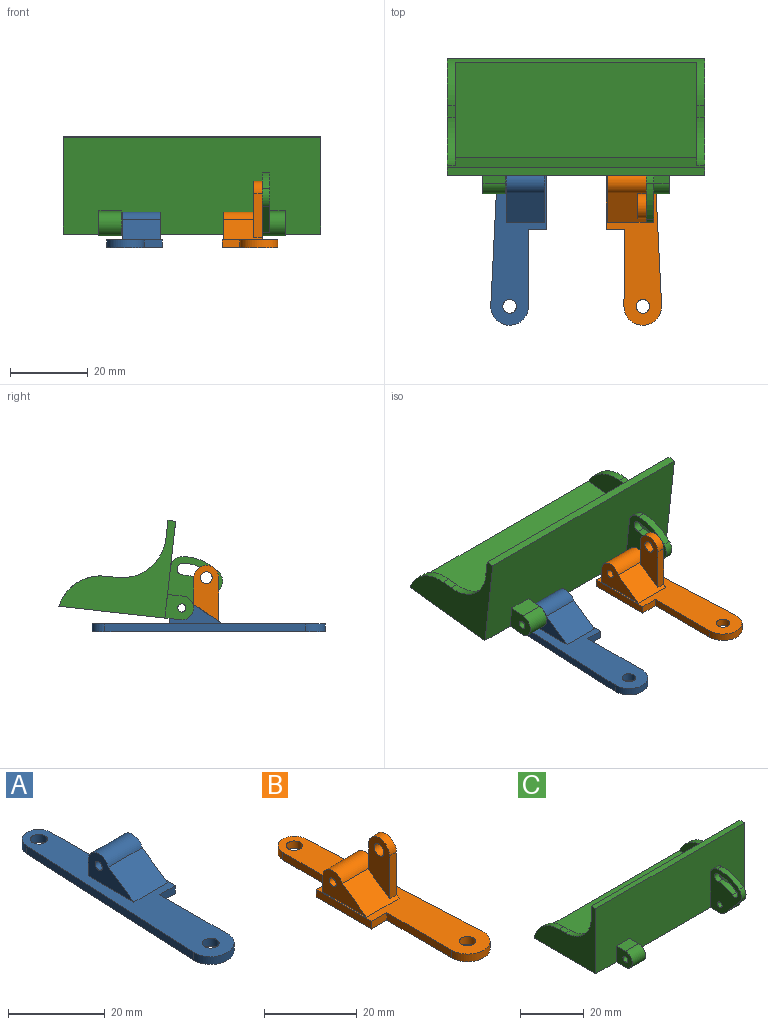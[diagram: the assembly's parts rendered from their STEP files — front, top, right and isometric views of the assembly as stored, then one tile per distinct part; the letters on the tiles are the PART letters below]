
ASSEMBLY  parts=3 mates=3
PART A: 18 faces, bbox 14.3x59.9x9.1 mm
  f0: plane 16.87x2mm, normal (1,0,0), area 33.7mm2, adj f1,f8,f10,f11
  f1: plane 4.68x2mm, normal (0,1,0), area 9.4mm2, adj f0,f2,f10,f11
  f2: plane 14.87x2mm, normal (1,0,0), area 29.7mm2, adj f1,f3,f10,f11
  f3: cylinder r=3.51mm len=7.01mm, axis (0,0,-1), area 21.7mm2, adj f2,f4,f10,f11
  f4: plane 51.47x2.53mm, normal (-1,0.05,0), area 103.1mm2, adj f3,f5,f10,f11
  f5: cylinder r=4.83mm len=9.67mm, axis (0,0,-1), area 30.9mm2, adj f4,f6,f10,f11
  f6: plane 19.79x2mm, normal (1,0,0), area 39.6mm2, adj f5,f8,f10,f11
  f7: cylinder r=1.75mm len=3.5mm, axis (0,0,-1), area 22mm2, adj f10,f11
  f8: plane 4.64x2mm, normal (0,-1,0), area 9.3mm2, adj f0,f6,f10,f11
  f9: cylinder r=1.75mm len=3.5mm, axis (0,0,-1), area 22mm2, adj f10,f11
  f10: plane 59.88x14.26mm, normal (0,0,1), area 413.1mm2, adj f0,f1,f2,f3,f4,f5,f6,f7
  f11: plane 59.88x14.26mm, normal (0,0,-1), area 545.5mm2, adj f0,f1,f2,f3,f4,f5,f6,f7
  f12: plane 9.9x4.05mm, normal (0,1,0), area 40.1mm2, adj f10,f14,f15,f16
  f13: cylinder r=1.05mm len=9.9mm, axis (1,0,0), area 65.3mm2, adj f15,f16
  f14: cylinder r=3.05mm len=9.9mm, axis (1,0,0), area 83.8mm2, adj f12,f15,f16,f17
  f15: plane 13.37x7.1mm, normal (-1,0,0), area 54.1mm2, adj f10,f12,f13,f14,f17
  f16: plane 13.37x7.1mm, normal (1,0,0), area 54.1mm2, adj f10,f12,f13,f14,f17
  f17: plane 9.9x7.47mm, normal (0,-0.57,0.82), area 89.8mm2, adj f10,f14,f15,f16
PART B: 23 faces, bbox 14.3x59.9x17 mm
  f0: plane 9.9x7.47mm, normal (0,-0.57,0.82), area 73.5mm2, adj f1,f15,f16,f17,f18,f19,f20
  f1: plane 59.88x14.26mm, normal (0,0,1), area 413.1mm2, adj f0,f2,f3,f4,f5,f6,f7,f8
  f2: plane 4.68x2mm, normal (0,1,0), area 9.4mm2, adj f1,f3,f10,f12
  f3: plane 16.87x2mm, normal (-1,0,0), area 33.7mm2, adj f1,f2,f4,f12
  f4: plane 4.64x2mm, normal (0,-1,0), area 9.3mm2, adj f1,f3,f5,f12
  f5: plane 19.79x2mm, normal (-1,0,0), area 39.6mm2, adj f1,f4,f6,f12
  f6: cylinder r=4.83mm len=9.67mm, axis (0,0,-1), area 30.9mm2, adj f1,f5,f7,f12
  f7: plane 51.47x2.53mm, normal (1,0.05,0), area 103.1mm2, adj f1,f6,f8,f12
  f8: cylinder r=3.51mm len=7.01mm, axis (0,0,-1), area 21.7mm2, adj f1,f7,f10,f12
  f9: cylinder r=1.75mm len=3.5mm, axis (0,0,-1), area 22mm2, adj f1,f12
  f10: plane 14.88x2mm, normal (-1,0,0), area 29.8mm2, adj f1,f2,f8,f12
  f11: cylinder r=1.75mm len=3.5mm, axis (0,0,-1), area 22mm2, adj f1,f12
  f12: plane 59.88x14.26mm, normal (0,0,-1), area 545.5mm2, adj f2,f3,f4,f5,f6,f7,f8,f9
  f13: plane 9.9x4.05mm, normal (0,1,0), area 40.1mm2, adj f1,f15,f16,f17
  f14: cylinder r=1.05mm len=9.9mm, axis (-1,0,0), area 65.3mm2, adj f16,f17
  f15: cylinder r=3.05mm len=9.9mm, axis (-1,0,0), area 83.8mm2, adj f0,f13,f16,f17
  f16: plane 15.02x13.37mm, normal (1,0,0), area 121mm2, adj f0,f1,f13,f14,f15,f18,f19,f21
  f17: plane 13.37x7.1mm, normal (-1,0,0), area 54.1mm2, adj f0,f1,f13,f14,f15
  f18: plane 6.85x2.1mm, normal (0,1,0), area 14.4mm2, adj f0,f16,f20,f21
  f19: plane 11.25x2.1mm, normal (0,-1,0), area 23.6mm2, adj f0,f16,f20,f21
  f20: plane 14.45x6.4mm, normal (-1,0,0), area 66.9mm2, adj f0,f18,f19,f21,f22
  f21: cylinder r=3.2mm len=6.4mm, axis (1,0,0), area 21.1mm2, adj f16,f18,f19,f20
  f22: cylinder r=1.5mm len=3mm, axis (1,0,0), area 19.8mm2, adj f16,f20
PART C: 33 faces, bbox 66x41.1x25 mm
  f0: plane 66x25mm, normal (0,-1,0), area 1564.2mm2, adj f1,f3,f4,f5,f7,f14,f15,f16
  f1: plane 4.05x3.9mm, normal (0,0,1), area 15.8mm2, adj f0,f12,f14,f32
  f2: plane 62x24.78mm, normal (0,0,1), area 1536.3mm2, adj f6,f8,f10,f22
  f3: plane 27.4x25mm, normal (-1,0,0), area 281mm2, adj f0,f5,f6,f7,f9,f22,f23
  f4: plane 27.4x25mm, normal (1,0,0), area 281mm2, adj f0,f5,f6,f7,f11,f21,f22
  f5: plane 66x31.45mm, normal (0,0,-1), area 1856.2mm2, adj f0,f3,f4,f12,f14,f15,f17,f19
  f6: plane 66x23mm, normal (0,1,0), area 1444.6mm2, adj f2,f3,f4,f7,f8,f10,f21,f23
  f7: plane 66x2mm, normal (0,0,1), area 132mm2, adj f0,f3,f4,f6
  f8: plane 24.78x18.35mm, normal (1,0,0), area 180.8mm2, adj f2,f6,f9,f22,f23
  f9: plane 2.95x2mm, normal (0,0,1), area 5.9mm2, adj f3,f8,f22,f23
  f10: plane 24.78x18.35mm, normal (-1,0,0), area 180.8mm2, adj f2,f6,f11,f21,f22
  f11: plane 2.95x2mm, normal (0,0,1), area 5.9mm2, adj f4,f10,f21,f22
  f12: cylinder r=3.05mm len=6.1mm, axis (-1,0,0), area 42.6mm2, adj f1,f5,f14,f15,f27,f32
  f13: cylinder r=1.05mm len=5.9mm, axis (-1,0,0), area 38.9mm2, adj f14,f15
  f14: plane 7.1x6.1mm, normal (1,0,0), area 35.9mm2, adj f0,f1,f5,f12,f13
  f15: plane 16.25x13.69mm, normal (-1,0,0), area 133.8mm2, adj f0,f5,f12,f13,f24,f25,f26,f27
  f16: plane 5.9x4.05mm, normal (0,0,1), area 23.9mm2, adj f0,f17,f19,f20
  f17: cylinder r=3.05mm len=6.1mm, axis (1,0,0), area 56.5mm2, adj f5,f16,f19,f20
  f18: cylinder r=1.05mm len=5.9mm, axis (1,0,0), area 38.9mm2, adj f19,f20
  f19: plane 7.1x6.1mm, normal (-1,0,0), area 35.9mm2, adj f0,f5,f16,f17,f18
  f20: plane 7.1x6.1mm, normal (1,0,0), area 35.9mm2, adj f0,f5,f16,f17,f18
  f21: cylinder r=11.35mm len=11.35mm, axis (-1,0,0), area 35.6mm2, adj f4,f6,f10,f11
  f22: cylinder r=11.35mm len=66mm, axis (-1,0,0), area 191.9mm2, adj f2,f3,f4,f5,f8,f9,f10,f11
  f23: cylinder r=11.35mm len=11.35mm, axis (1,0,0), area 35.6mm2, adj f3,f6,f8,f9
  f24: cylinder r=11.5mm len=8.39mm, axis (-1,0,0), area 18.1mm2, adj f15,f25,f31,f32
  f25: cylinder r=1.5mm len=2.65mm, axis (-1,0,0), area 9.4mm2, adj f15,f24,f26,f32
  f26: cylinder r=8.5mm len=6.2mm, axis (-1,0,0), area 13.4mm2, adj f15,f25,f31,f32
  f27: plane 7.55x6.56mm, normal (0,-0.75,-0.66), area 20mm2, adj f12,f15,f28,f32
  f28: cylinder r=3.2mm len=4.55mm, axis (-1,0,0), area 10.1mm2, adj f15,f27,f29,f32
  f29: cylinder r=13.2mm len=9.63mm, axis (-1,0,0), area 20.7mm2, adj f15,f28,f30,f32
  f30: cylinder r=3.2mm len=3.19mm, axis (-1,0,0), area 9.5mm2, adj f0,f15,f29,f32
  f31: cylinder r=1.5mm len=2.99mm, axis (-1,0,0), area 9.4mm2, adj f15,f24,f26,f32
  f32: plane 15.2x13.69mm, normal (1,0,0), area 97.9mm2, adj f0,f1,f12,f24,f25,f26,f27,f28
PLACE A rot(axis=(1,0,0),0deg) t=(-17.05,-30.02,-22)mm
PLACE B rot(axis=(1,0,0),0deg) t=(-16.95,-30.02,-22)mm
PLACE C rot(axis=(1,0,0),6.4deg) t=(-17.05,50.95,3.1)mm
MATE revolute C.f12 <-> B.f14  axis (-1,0,0) through (0.95,31.98,4.05)mm
MATE planar A.f10 <-> B.f1  axis (0,0,1) through (-33.45,22.8,0)mm
MATE revolute A.f13 <-> C.f12  axis (-1,0,0) through (-34.95,31.98,4.05)mm
